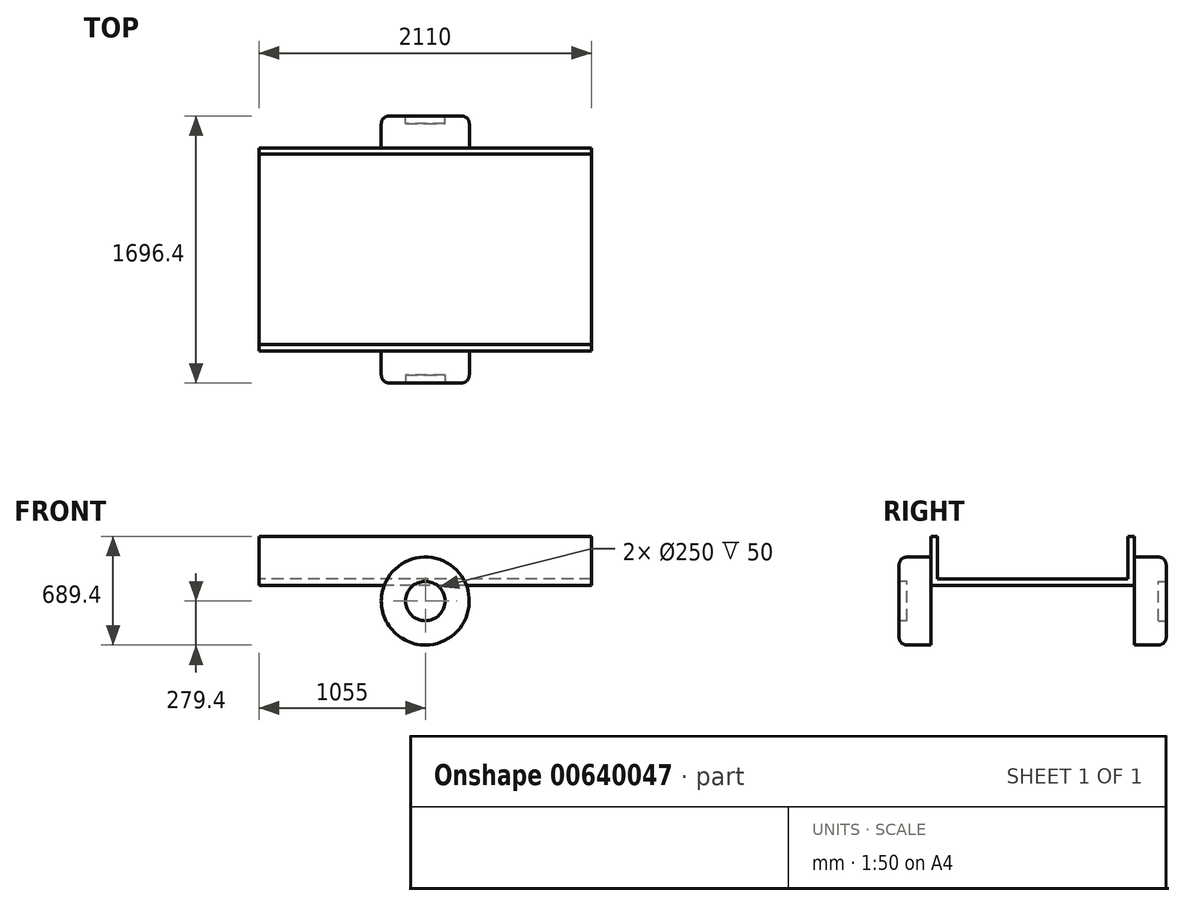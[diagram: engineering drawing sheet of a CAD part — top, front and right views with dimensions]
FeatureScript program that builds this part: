
annotation { "Feature Type Name" : "Feature", "Feature Type Description" : "" }
export const myFeature = defineFeature(function(context is Context, id is Id, definition is map)
    precondition{}
    {
        {
            var Q0;
            Q0=qCreatedBy(makeId("Top.planeOp"),FACE);
            var sketch = newSketch(context, id + "F0", { "sketchPlane" : qUnion([Q0])});
            skLineSegment(sketch, "E0.bottom", {"start": v(1055, 645) * mm, "end": v(-1055, 645) * mm});
            skLineSegment(sketch, "E0.top", {"start": v(1055, -645) * mm, "end": v(-1055, -645) * mm});
            skLineSegment(sketch, "E0.left", {"start": v(1055, 645) * mm, "end": v(1055, -645) * mm});
            skLineSegment(sketch, "E0.right", {"start": v(-1055, 645) * mm, "end": v(-1055, -645) * mm});
            skPoint(sketch, "E0.middle", {"position": v(0, 0) * mm});
            skSolve(sketch);
        }
        {
            var Q0;
            Q0=makeQuery(id+"F0.imprint","IMPRINT",FACE,{"disambiguationData":[TD([[makeQuery(id+"F0.imprint","IMPRINT",EDGE,{"derivedFrom":sQuery(id+"F0.wireOp",EDGE,"E0.bottom")}),1.0]])]});
            extrude(context, id + "F1", {"entities" : qUnion([Q0]), "depth" : 310 * mm, "offsetDistance" : 25 * mm});
        }
        {
            var Q0;
            Q0=makeQuery(id+"F1.opExtrude","SWEPT_FACE",FACE,{"disambiguationData":[OSD([sQuery(id+"F0.wireOp",EDGE,"E0.left")])]});
            var Q1;
            Q1=makeQuery(id+"F1.opExtrude","CAP_FACE",FACE,{"disambiguationData":[OSD([sQuery(id+"F0.wireOp",EDGE,"E0.bottom"),sQuery(id+"F0.wireOp",EDGE,"E0.top"),sQuery(id+"F0.wireOp",EDGE,"E0.left"),sQuery(id+"F0.wireOp",EDGE,"E0.right")])],"isStart":false});
            var Q2;
            Q2=makeQuery(id+"F1.opExtrude","SWEPT_FACE",FACE,{"disambiguationData":[OSD([sQuery(id+"F0.wireOp",EDGE,"E0.right")])]});
            shell(context, id + "F2", {"entities" : qUnion([Q0, Q1, Q2]), "thickness" : 40 * mm});
        }
        {
            var Q0;
            Q0=makeQuery(id+"F1.opExtrude","SWEPT_FACE",FACE,{"disambiguationData":[OSD([sQuery(id+"F0.wireOp",EDGE,"E0.top")])]});
            var sketch = newSketch(context, id + "F3", { "sketchPlane" : qUnion([Q0])});
            skCircle(sketch, "E1", {"center": v(0, -100) * mm, "radius": 279.4 * mm});
            skLineSegment(sketch, "E2", {"start": v(0, 0) * mm, "end": v(0, -100) * mm, "construction": true});
            skSolve(sketch);
        }
        {
            var Q0;
            {var subQ0=sQuery(id+"F3.wireOp",EDGE,"E1");var subQ1=makeQuery(id+"F1.opExtrude","CAP_EDGE",EDGE,{"disambiguationData":[OSD([sQuery(id+"F0.wireOp",EDGE,"E0.top")])],"isStart":true});var subQ2=makeQuery(id+"F3.imprint","INTERSECT",VERTEX,{"disambiguationData":[OD(0.0)],"derivedFrom":[subQ1,subQ0]});Q0=makeQuery(id+"F3.imprint","IMPRINT",FACE,{"disambiguationData":[TD([[makeQuery(id+"F3.imprint","IMPRINT",EDGE,{"disambiguationData":[TD([[subQ2,-1.0]])],"derivedFrom":subQ0}),1.0]])]});}
            var Q1;
            {var subQ0=sQuery(id+"F3.wireOp",EDGE,"E1");var subQ1=makeQuery(id+"F1.opExtrude","CAP_EDGE",EDGE,{"disambiguationData":[OSD([sQuery(id+"F0.wireOp",EDGE,"E0.top")])],"isStart":true});var subQ2=makeQuery(id+"F3.imprint","INTERSECT",VERTEX,{"disambiguationData":[OD(0.0)],"derivedFrom":[subQ1,subQ0]});Q1=makeQuery(id+"F3.imprint","IMPRINT",FACE,{"disambiguationData":[TD([[makeQuery(id+"F3.imprint","IMPRINT",EDGE,{"disambiguationData":[TD([[subQ2,1.0]])],"derivedFrom":subQ0}),1.0]])]});}
            extrude(context, id + "F4", {"entities" : qUnion([Q0, Q1]), "operationType" : NewBodyOperationType.ADD, "depth" : 203.2 * mm, "offsetDistance" : 25 * mm});
        }
        {
            var Q0;
            Q0=makeQuery(id+"F4.opExtrude","CAP_EDGE",EDGE,{"disambiguationData":[OSD([sQuery(id+"F3.wireOp",EDGE,"E1")])],"isStart":false});
            fillet(context, id + "F5", {"entities" : qUnion([Q0]), "radius" : 50 * mm, "tangentPropagation" : true, "allowEdgeOverflow" : false});
        }
        {
            var Q0;
            Q0=makeQuery(id+"F4.opExtrude","CAP_FACE",FACE,{"disambiguationData":[OSD([sQuery(id+"F3.wireOp",EDGE,"E1")])],"isStart":false});
            var sketch = newSketch(context, id + "F6", { "sketchPlane" : qUnion([Q0])});
            skCircle(sketch, "E3", {"center": v(0, -100) * mm, "radius": 125 * mm});
            skSolve(sketch);
        }
        {
            var Q0;
            Q0=makeQuery(id+"F6.imprint","IMPRINT",FACE,{"disambiguationData":[TD([[makeQuery(id+"F6.imprint","IMPRINT",EDGE,{"derivedFrom":sQuery(id+"F6.wireOp",EDGE,"E3")}),1.0]])]});
            extrude(context, id + "F7", {"entities" : qUnion([Q0]), "operationType" : NewBodyOperationType.REMOVE, "oppositeDirection" : true, "depth" : 50 * mm, "offsetDistance" : 25 * mm});
        }
        {
            var Q0;
            Q0=makeQuery(id+"F1.opExtrude","SWEPT_BODY",BODY,{"disambiguationData":[OSD([sQuery(id+"F0.wireOp",EDGE,"E0.bottom"),sQuery(id+"F0.wireOp",EDGE,"E0.top"),sQuery(id+"F0.wireOp",EDGE,"E0.left"),sQuery(id+"F0.wireOp",EDGE,"E0.right")])]});
            var Q1;
            Q1=qCreatedBy(makeId("Front.planeOp"),FACE);
            mirror(context, id + "F8", {"operationType" : NewBodyOperationType.ADD, "entities" : qUnion([Q0]), "mirrorPlane" : qUnion([Q1])});
        }
    });
